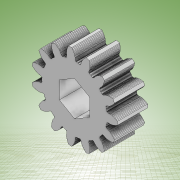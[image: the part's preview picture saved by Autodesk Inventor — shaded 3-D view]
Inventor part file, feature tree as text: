
AUTODESK INVENTOR PART (.ipt)
format: ipt  version: 2022 (Build 260153000, 153)  size: 1,249,280 bytes
history: native  units: mm
features: other x1, extrude x1, sketch x1
ambient origin geometry x8: Origin, YZ Plane, XZ Plane, XY Plane, X Axis, Y Axis, Z Axis, Center Point
bodies: Body1 (feature_tree)
feature tree (3):
  other  "Sólido1"
  extrude  "Extrusión1"  Depth=6.0mm TaperAngle=0.0deg
  sketch  "Boceto1"  dims[d0=6.0mm d3=6.0mm d4=0.0mm]
